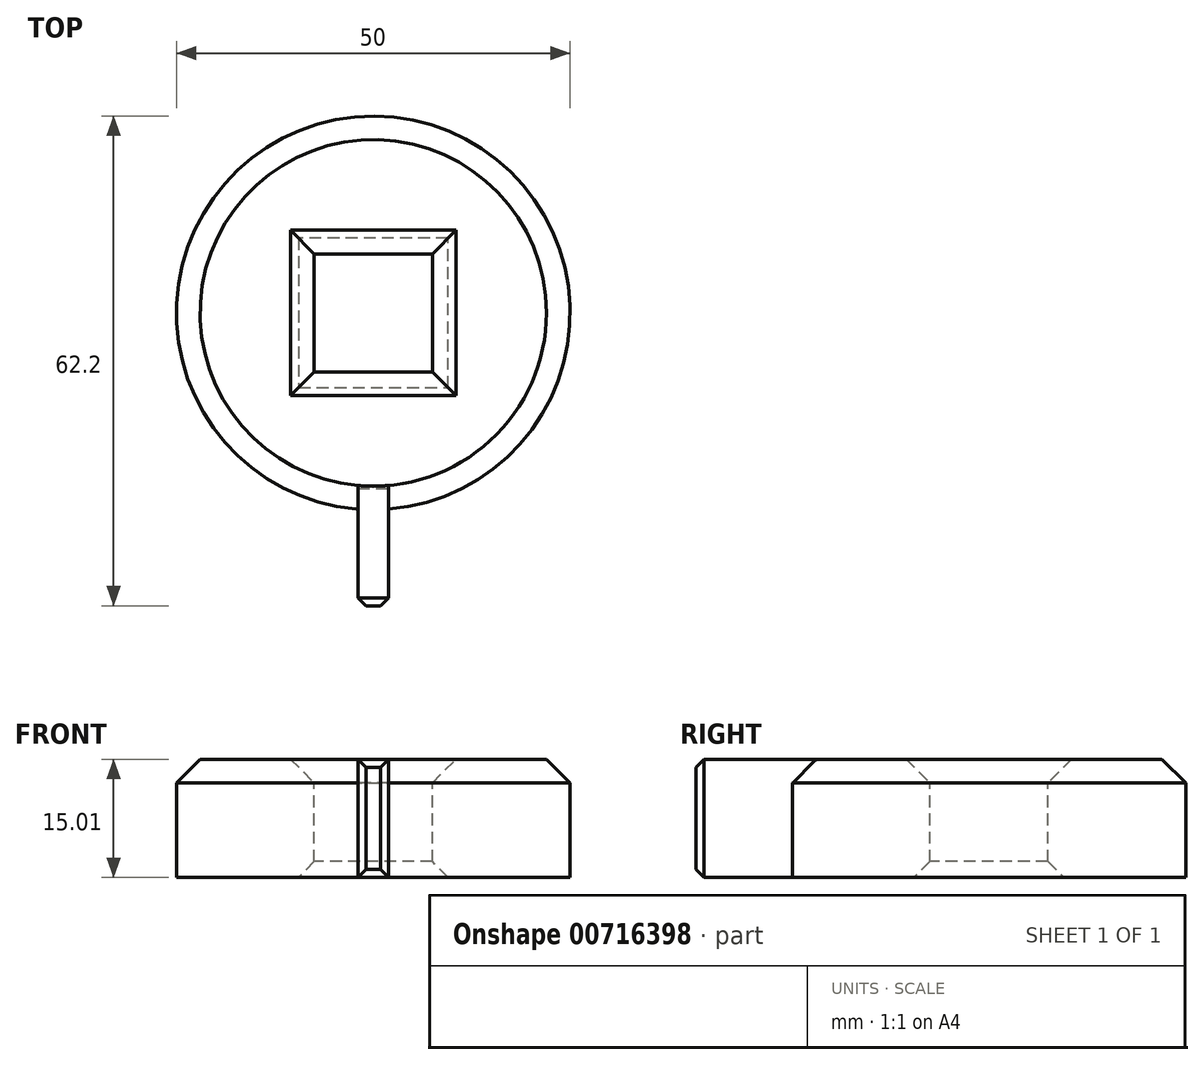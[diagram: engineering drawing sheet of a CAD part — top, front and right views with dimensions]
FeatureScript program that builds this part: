
annotation { "Feature Type Name" : "Feature", "Feature Type Description" : "" }
export const myFeature = defineFeature(function(context is Context, id is Id, definition is map)
    precondition{}
    {
        {
            var Q0;
            Q0=qCreatedBy(makeId("Top.planeOp"),FACE);
            var sketch = newSketch(context, id + "F0", { "sketchPlane" : qUnion([Q0])});
            skCircle(sketch, "E0", {"center": v(0, 0) * mm, "radius": 25 * mm});
            skSolve(sketch);
        }
        {
            var Q0;
            Q0=makeQuery(id+"F0.imprint","IMPRINT",FACE,{"disambiguationData":[TD([[makeQuery(id+"F0.imprint","IMPRINT",EDGE,{"derivedFrom":sQuery(id+"F0.wireOp",EDGE,"E0")}),1.0]])]});
            extrude(context, id + "F1", {"entities" : qUnion([Q0]), "depth" : 15 * mm, "offsetDistance" : 25 * mm});
        }
        {
            var Q0;
            Q0=makeQuery(id+"F1.opExtrude","CAP_FACE",FACE,{"disambiguationData":[OSD([sQuery(id+"F0.wireOp",EDGE,"E0")])],"isStart":false});
            var sketch = newSketch(context, id + "F2", { "sketchPlane" : qUnion([Q0])});
            skLineSegment(sketch, "E1.bottom", {"start": v(7.5, -7.5) * mm, "end": v(-7.5, -7.5) * mm});
            skLineSegment(sketch, "E1.top", {"start": v(7.5, 7.5) * mm, "end": v(-7.5, 7.5) * mm});
            skLineSegment(sketch, "E1.left", {"start": v(7.5, -7.5) * mm, "end": v(7.5, 7.5) * mm});
            skLineSegment(sketch, "E1.right", {"start": v(-7.5, -7.5) * mm, "end": v(-7.5, 7.5) * mm});
            skPoint(sketch, "E1.middle", {"position": v(0, 0) * mm});
            skSolve(sketch);
        }
        {
            var Q0;
            Q0=makeQuery(id+"F2.imprint","IMPRINT",FACE,{"disambiguationData":[TD([[makeQuery(id+"F2.imprint","IMPRINT",EDGE,{"derivedFrom":sQuery(id+"F2.wireOp",EDGE,"E1.bottom")}),-1.0]])]});
            extrude(context, id + "F3", {"entities" : qUnion([Q0]), "operationType" : NewBodyOperationType.REMOVE, "oppositeDirection" : true, "depth" : 25 * mm, "offsetDistance" : 25 * mm});
        }
        {
            var Q0;
            Q0=qCreatedBy(makeId("Front.planeOp"),FACE);
            cPlane(context, id + "F4", {"entities" : qUnion([Q0]), "cplaneType" : CPlaneType.OFFSET, "offset" : 25 * mm, "width" : 150 * mm, "height" : 150 * mm});
        }
        {
            var Q0;
            Q0=qCreatedBy(id+"F4.planeOp",FACE);
            var sketch = newSketch(context, id + "F5", { "sketchPlane" : qUnion([Q0])});
            skLineSegment(sketch, "E2.bottom", {"start": v(1.95, -0.01) * mm, "end": v(-1.95, -0.01) * mm});
            skLineSegment(sketch, "E2.top", {"start": v(1.95, 14.98) * mm, "end": v(-1.95, 14.98) * mm});
            skLineSegment(sketch, "E2.left", {"start": v(1.95, -0.01) * mm, "end": v(1.95, 14.98) * mm});
            skLineSegment(sketch, "E2.right", {"start": v(-1.95, -0.01) * mm, "end": v(-1.95, 14.98) * mm});
            skPoint(sketch, "E2.middle", {"position": v(0, 7.48) * mm});
            skSolve(sketch);
        }
        {
            var Q0;
            Q0=makeQuery(id+"F5.imprint","IMPRINT",FACE,{"disambiguationData":[TD([[makeQuery(id+"F5.imprint","IMPRINT",EDGE,{"derivedFrom":sQuery(id+"F5.wireOp",EDGE,"E2.bottom")}),-1.0]])]});
            extrude(context, id + "F6", {"entities" : qUnion([Q0]), "operationType" : NewBodyOperationType.ADD, "depth" : 12.2 * mm, "offsetDistance" : 25 * mm, "hasSecondDirection" : true, "secondDirectionOppositeDirection" : true, "secondDirectionDepth" : 2.7 * mm});
        }
        {
            var Q0;
            Q0=makeQuery(id+"F6.opExtrude","CAP_FACE",FACE,{"disambiguationData":[OSD([sQuery(id+"F5.wireOp",EDGE,"E2.bottom"),sQuery(id+"F5.wireOp",EDGE,"E2.top"),sQuery(id+"F5.wireOp",EDGE,"E2.left"),sQuery(id+"F5.wireOp",EDGE,"E2.right")])],"isStart":false});
            chamfer(context, id + "F7", {"entities" : qUnion([Q0]), "width" : 1 * mm, "tangentPropagation" : true});
        }
        {
            var Q0;
            Q0=makeQuery(id+"F1.opExtrude","CAP_FACE",FACE,{"disambiguationData":[OSD([sQuery(id+"F0.wireOp",EDGE,"E0")])],"isStart":false});
            chamfer(context, id + "F8", {"entities" : qUnion([Q0]), "width" : 3 * mm, "tangentPropagation" : true});
        }
        {
            var Q0;
            Q0=makeQuery(id+"F3.boolean.opBoolean","INTERSECT",EDGE,{"derivedFrom":[makeQuery(id+"F1.opExtrude","CAP_FACE",FACE,{"disambiguationData":[OSD([sQuery(id+"F0.wireOp",EDGE,"E0")])],"isStart":true}),makeQuery(id+"F3.opExtrude","SWEPT_FACE",FACE,{"disambiguationData":[OSD([sQuery(id+"F2.wireOp",EDGE,"E1.bottom")])]})]});
            var Q1;
            Q1=makeQuery(id+"F3.boolean.opBoolean","INTERSECT",EDGE,{"derivedFrom":[makeQuery(id+"F1.opExtrude","CAP_FACE",FACE,{"disambiguationData":[OSD([sQuery(id+"F0.wireOp",EDGE,"E0")])],"isStart":true}),makeQuery(id+"F3.opExtrude","SWEPT_FACE",FACE,{"disambiguationData":[OSD([sQuery(id+"F2.wireOp",EDGE,"E1.right")])]})]});
            var Q2;
            Q2=makeQuery(id+"F3.boolean.opBoolean","INTERSECT",EDGE,{"derivedFrom":[makeQuery(id+"F1.opExtrude","CAP_FACE",FACE,{"disambiguationData":[OSD([sQuery(id+"F0.wireOp",EDGE,"E0")])],"isStart":true}),makeQuery(id+"F3.opExtrude","SWEPT_FACE",FACE,{"disambiguationData":[OSD([sQuery(id+"F2.wireOp",EDGE,"E1.top")])]})]});
            var Q3;
            Q3=makeQuery(id+"F3.boolean.opBoolean","INTERSECT",EDGE,{"derivedFrom":[makeQuery(id+"F1.opExtrude","CAP_FACE",FACE,{"disambiguationData":[OSD([sQuery(id+"F0.wireOp",EDGE,"E0")])],"isStart":true}),makeQuery(id+"F3.opExtrude","SWEPT_FACE",FACE,{"disambiguationData":[OSD([sQuery(id+"F2.wireOp",EDGE,"E1.left")])]})]});
            chamfer(context, id + "F9", {"entities" : qUnion([Q0, Q1, Q2, Q3]), "width" : 2 * mm, "tangentPropagation" : true});
        }
    });
